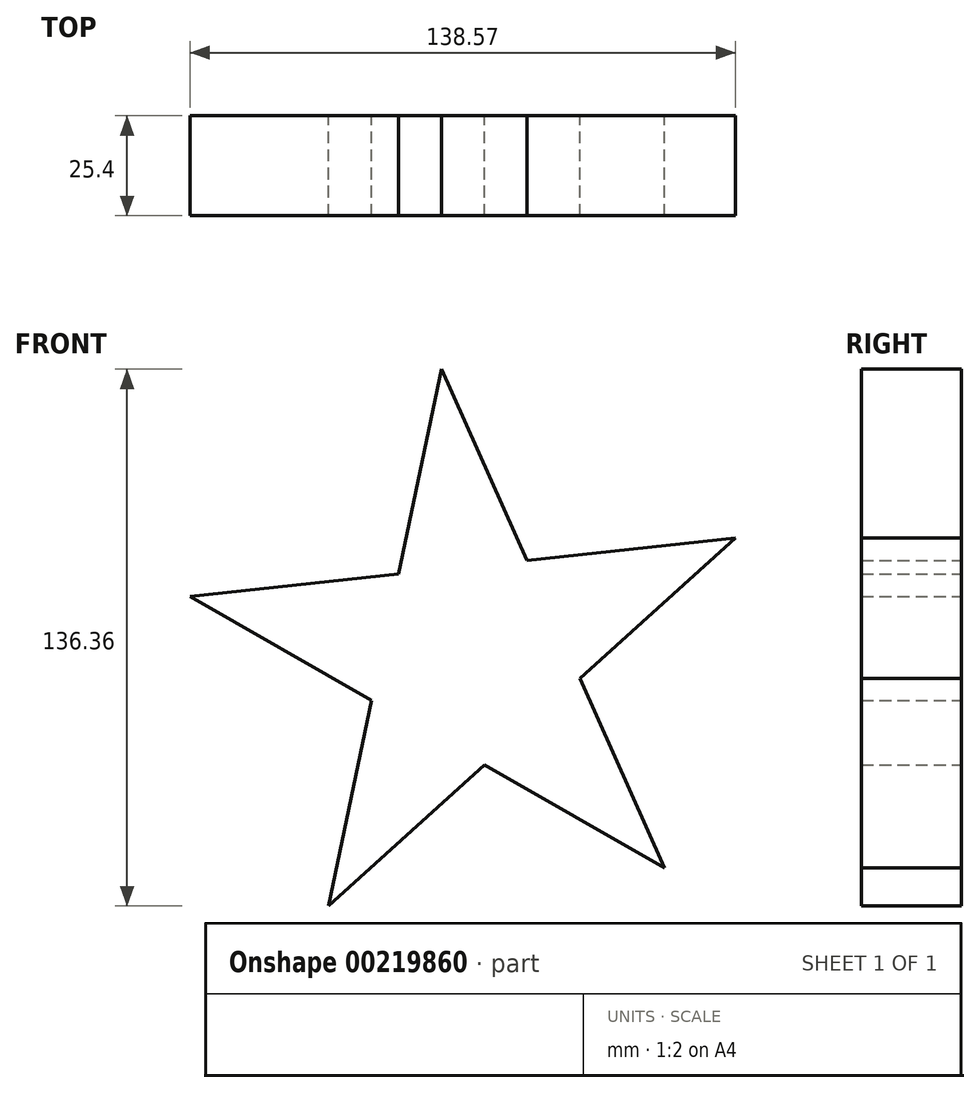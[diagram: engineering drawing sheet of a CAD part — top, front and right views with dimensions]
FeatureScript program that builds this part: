
annotation { "Feature Type Name" : "Feature", "Feature Type Description" : "" }
export const myFeature = defineFeature(function(context is Context, id is Id, definition is map)
    precondition{}
    {
        {
            var Q0;
            Q0=qCreatedBy(makeId("Front.planeOp"),FACE);
            var sketch = newSketch(context, id + "F0", { "sketchPlane" : qUnion([Q0])});
            skLineSegment(sketch, "E0.1", {"start": v(49.18, -54.02) * mm, "end": v(49.1, -54.37) * mm});
            skPoint(sketch, "E0.0.midPoint", {"position": v(29.56, 51.38) * mm});
            skLineSegment(sketch, "E1", {"start": v(-36.53, -63.5) * mm, "end": v(3.13, -27.68) * mm});
            skLineSegment(sketch, "E2", {"start": v(-7.77, 72.85) * mm, "end": v(13.95, 24.26) * mm});
            skLineSegment(sketch, "E3", {"start": v(49.41, -54.15) * mm, "end": v(3.13, -27.68) * mm});
            skLineSegment(sketch, "E4", {"start": v(-71.69, 15.12) * mm, "end": v(-18.76, 20.77) * mm});
            skLineSegment(sketch, "E5", {"start": v(-7.77, 72.85) * mm, "end": v(-18.76, 20.77) * mm});
            skLineSegment(sketch, "E6.trimOffspring", {"start": v(27.38, -5.78) * mm, "end": v(66.88, 29.9) * mm});
            skLineSegment(sketch, "E7.trimOffspring", {"start": v(-25.52, -11.29) * mm, "end": v(-36.53, -63.5) * mm});
            skLineSegment(sketch, "E8.trimOffspring", {"start": v(-25.52, -11.29) * mm, "end": v(-71.69, 15.12) * mm});
            skLineSegment(sketch, "E9.trimOffspring", {"start": v(13.95, 24.26) * mm, "end": v(66.88, 29.9) * mm});
            skLineSegment(sketch, "E10.trimOffspring", {"start": v(27.38, -5.78) * mm, "end": v(49.1, -54.37) * mm});
            skSolve(sketch);
        }
        {
            var Q0;
            {var subQ1=sQuery(id+"F0.wireOp",EDGE,"E1");Q0=makeQuery(id+"F0.imprint","IMPRINT",FACE,{"disambiguationData":[TD([[makeQuery(id+"F0.imprint","IMPRINT",EDGE,{"derivedFrom":subQ1}),1.0]])]});}
            extrude(context, id + "F1", {"entities" : qUnion([Q0]), "depth" : 25.4 * mm});
        }
    });
